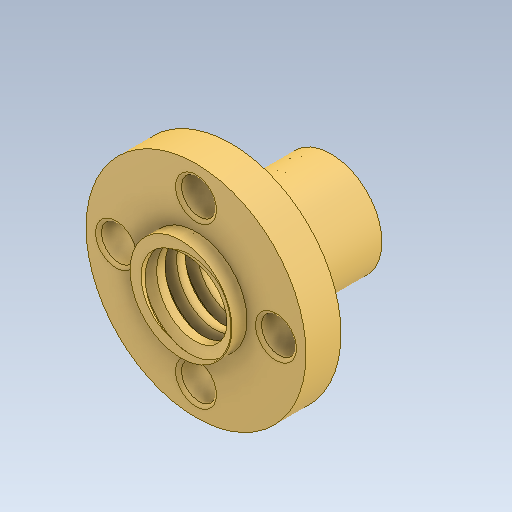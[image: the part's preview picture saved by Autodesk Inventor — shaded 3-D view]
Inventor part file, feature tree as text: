
AUTODESK INVENTOR PART (.ipt)
format: ipt  version: 2020 (Build 240168000, 168)  size: 288,256 bytes
history: mixed  units: in
note: dims shown in document units (in); Inventor stores cm internally (conversion verified against a paired STEP export)
features: fillet x1, imported_body x1
ambient origin geometry x8: Origin, YZ Plane, XZ Plane, XY Plane, X Axis, Y Axis, Z Axis, Center Point
bodies: Solid1 (imported_parasolid)
feature tree (2):
  fillet  "Fillet2"  [1 undecoded]
  imported_body  NMx_Import_Brep_tag  [imported B-rep: ~6 faces, bbox_mm=None]
note: 1 required parameter value undecoded (feature->parameter linkage not recoverable at this tier; creation-order binding heuristic only, values carry confidence <= 0.55)
